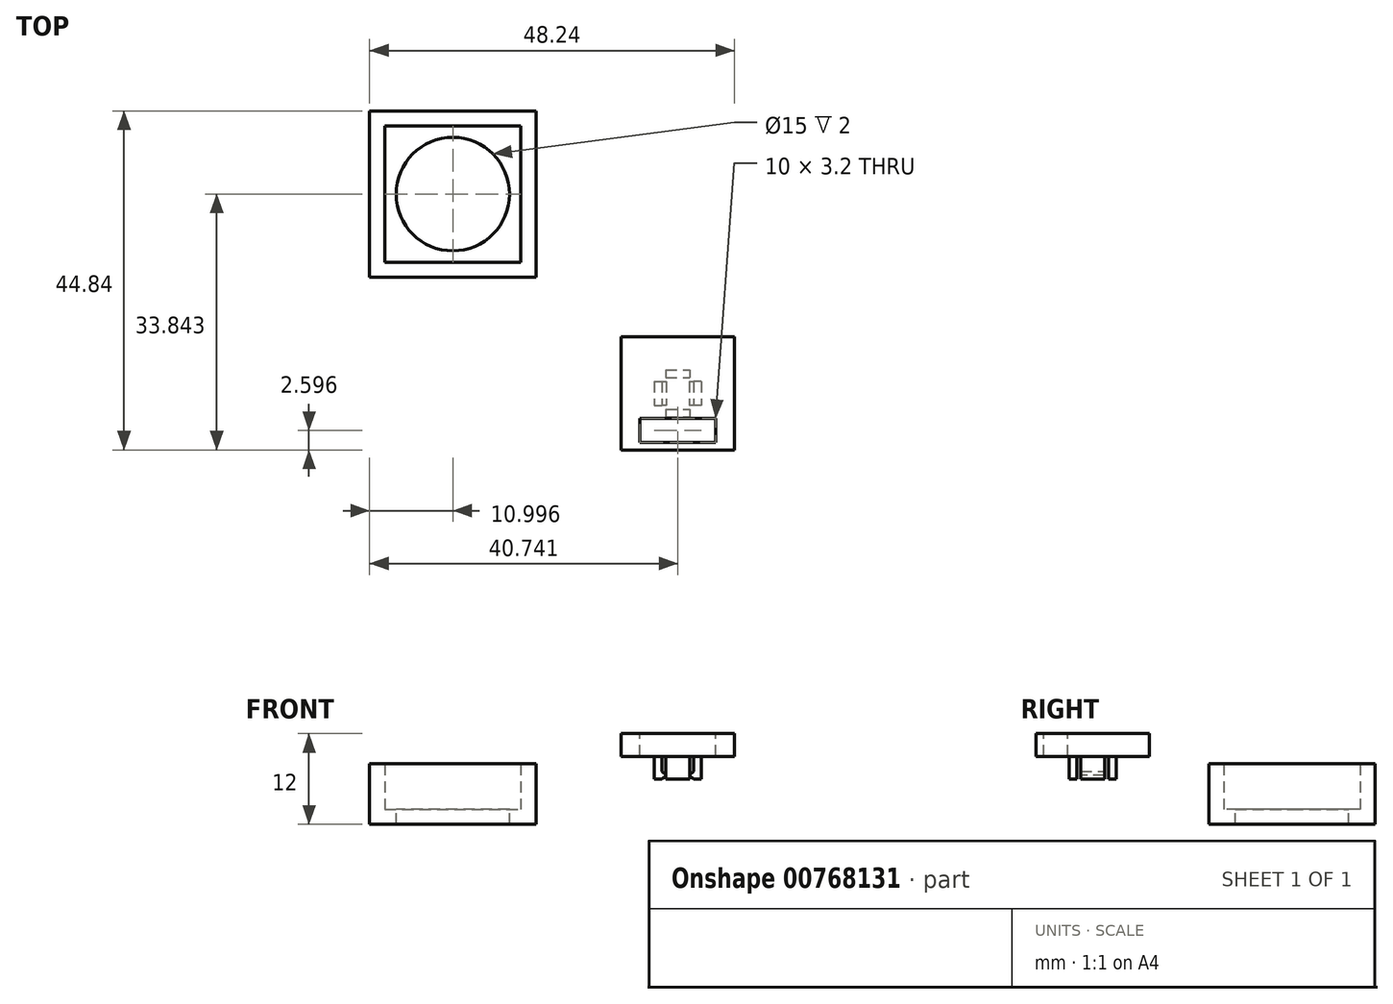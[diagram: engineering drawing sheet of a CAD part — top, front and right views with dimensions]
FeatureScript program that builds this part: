
annotation { "Feature Type Name" : "Feature", "Feature Type Description" : "" }
export const myFeature = defineFeature(function(context is Context, id is Id, definition is map)
    precondition{}
    {
        {
            var Q0;
            Q0=qCreatedBy(makeId("Top.planeOp"),FACE);
            var sketch = newSketch(context, id + "F0", { "sketchPlane" : qUnion([Q0])});
            skCircle(sketch, "E0", {"center": v(-35.06, 11.64) * mm, "radius": 7.5 * mm});
            skLineSegment(sketch, "E1", {"start": v(-38.26, 11.64) * mm, "end": v(-31.97, 11.64) * mm, "construction": true});
            skLineSegment(sketch, "E2", {"start": v(-35.06, 15.87) * mm, "end": v(-35.06, 7.55) * mm, "construction": true});
            skLineSegment(sketch, "E3.bottom", {"start": v(-44.06, 20.64) * mm, "end": v(-26.06, 20.64) * mm});
            skLineSegment(sketch, "E3.top", {"start": v(-44.06, 2.64) * mm, "end": v(-26.06, 2.64) * mm});
            skLineSegment(sketch, "E3.left", {"start": v(-44.06, 20.64) * mm, "end": v(-44.06, 2.64) * mm});
            skLineSegment(sketch, "E3.right", {"start": v(-26.06, 20.64) * mm, "end": v(-26.06, 2.64) * mm});
            skLineSegment(sketch, "E4.bottom", {"start": v(-46.06, 22.64) * mm, "end": v(-24.06, 22.64) * mm});
            skLineSegment(sketch, "E4.top", {"start": v(-46.06, 0.64) * mm, "end": v(-24.06, 0.64) * mm});
            skLineSegment(sketch, "E4.left", {"start": v(-46.06, 22.64) * mm, "end": v(-46.06, 0.64) * mm});
            skLineSegment(sketch, "E4.right", {"start": v(-24.06, 22.64) * mm, "end": v(-24.06, 0.64) * mm});
            skSolve(sketch);
        }
        {
            var Q0;
            Q0=makeQuery(id+"F0.imprint","IMPRINT",FACE,{"disambiguationData":[TD([[makeQuery(id+"F0.imprint","IMPRINT",EDGE,{"derivedFrom":sQuery(id+"F0.wireOp",EDGE,"P6zJFxaA-fPif-yFot-hNpY-F2ilPQpi4qHW.bottom")}),1.0]])]});
            var Q1;
            Q1=makeQuery(id+"F0.imprint","IMPRINT",FACE,{"disambiguationData":[TD([[makeQuery(id+"F0.imprint","IMPRINT",EDGE,{"derivedFrom":sQuery(id+"F0.wireOp",EDGE,"E0")}),-1.0]])]});
            var Q2;
            Q2=makeQuery(id+"F0.imprint","IMPRINT",FACE,{"disambiguationData":[TD([[makeQuery(id+"F0.imprint","IMPRINT",EDGE,{"derivedFrom":sQuery(id+"F0.wireOp",EDGE,"E3.bottom")}),1.0]])]});
            extrude(context, id + "F1", {"entities" : qUnion([Q0, Q1, Q2]), "oppositeDirection" : true, "depth" : 2 * mm, "offsetDistance" : 25 * mm});
        }
        {
            var Q0;
            Q0=makeQuery(id+"F0.imprint","IMPRINT",FACE,{"disambiguationData":[TD([[makeQuery(id+"F0.imprint","IMPRINT",EDGE,{"derivedFrom":sQuery(id+"F0.wireOp",EDGE,"E3.bottom")}),1.0]])]});
            extrude(context, id + "F2", {"entities" : qUnion([Q0]), "operationType" : NewBodyOperationType.ADD, "depth" : 6 * mm, "offsetDistance" : 25 * mm});
        }
        {
            var Q0;
            Q0=qCreatedBy(makeId("Top.planeOp"),FACE);
            var sketch = newSketch(context, id + "F3", { "sketchPlane" : qUnion([Q0])});
            skLineSegment(sketch, "E5.bottom", {"start": v(-7.32, -12.7) * mm, "end": v(-3.32, -12.7) * mm, "construction": true});
            skLineSegment(sketch, "E5.top", {"start": v(-7.32, -16.7) * mm, "end": v(-3.32, -16.7) * mm, "construction": true});
            skLineSegment(sketch, "E5.left", {"start": v(-7.32, -12.7) * mm, "end": v(-7.32, -16.7) * mm, "construction": true});
            skLineSegment(sketch, "E5.right", {"start": v(-3.32, -12.7) * mm, "end": v(-3.32, -16.7) * mm, "construction": true});
            skLineSegment(sketch, "E6.bottom", {"start": v(-12.82, -7.2) * mm, "end": v(2.18, -7.2) * mm});
            skLineSegment(sketch, "E6.top", {"start": v(-12.82, -22.2) * mm, "end": v(2.18, -22.2) * mm});
            skLineSegment(sketch, "E6.left", {"start": v(-12.82, -7.2) * mm, "end": v(-12.82, -22.2) * mm});
            skLineSegment(sketch, "E6.right", {"start": v(2.18, -7.2) * mm, "end": v(2.18, -22.2) * mm});
            skLineSegment(sketch, "E7", {"start": v(-5.32, -2.75) * mm, "end": v(-5.32, -34.44) * mm, "construction": true});
            skLineSegment(sketch, "E8", {"start": v(9.88, -14.7) * mm, "end": v(-20.88, -14.7) * mm, "construction": true});
            skCircle(sketch, "E9", {"center": v(-5.32, -19.6) * mm, "radius": 1.5 * mm, "construction": true});
            skLineSegment(sketch, "E10.bottom", {"start": v(-10.32, -18) * mm, "end": v(-0.32, -18) * mm});
            skLineSegment(sketch, "E10.top", {"start": v(-10.32, -21.2) * mm, "end": v(-0.32, -21.2) * mm});
            skLineSegment(sketch, "E10.left", {"start": v(-10.32, -18) * mm, "end": v(-10.32, -21.2) * mm});
            skLineSegment(sketch, "E10.right", {"start": v(-0.32, -18) * mm, "end": v(-0.32, -21.2) * mm});
            skLineSegment(sketch, "E11", {"start": v(4.65, -19.6) * mm, "end": v(-12.26, -19.6) * mm, "construction": true});
            skLineSegment(sketch, "E12.bottom", {"start": v(-8.42, -13.1) * mm, "end": v(-7.42, -13.1) * mm});
            skLineSegment(sketch, "E12.top", {"start": v(-8.42, -16.3) * mm, "end": v(-7.42, -16.3) * mm});
            skLineSegment(sketch, "E12.left", {"start": v(-8.42, -13.1) * mm, "end": v(-8.42, -16.3) * mm});
            skLineSegment(sketch, "E12.right", {"start": v(-7.42, -13.1) * mm, "end": v(-7.42, -16.3) * mm});
            skLineSegment(sketch, "E13.bottom", {"start": v(-6.92, -11.6) * mm, "end": v(-3.72, -11.6) * mm});
            skLineSegment(sketch, "E13.top", {"start": v(-6.92, -12.6) * mm, "end": v(-3.72, -12.6) * mm});
            skLineSegment(sketch, "E13.left", {"start": v(-3.72, -11.6) * mm, "end": v(-3.72, -12.6) * mm});
            skLineSegment(sketch, "E13.right", {"start": v(-6.92, -11.6) * mm, "end": v(-6.92, -12.6) * mm});
            skLineSegment(sketch, "E14.MirrorCS", {"start": v(-6.92, -16.8) * mm, "end": v(-3.72, -16.8) * mm});
            skLineSegment(sketch, "E15.MirrorCS", {"start": v(-6.92, -17.8) * mm, "end": v(-6.92, -16.8) * mm});
            skLineSegment(sketch, "E16.MirrorCS", {"start": v(-6.92, -17.8) * mm, "end": v(-3.72, -17.8) * mm});
            skLineSegment(sketch, "E17.MirrorCS", {"start": v(-3.72, -17.8) * mm, "end": v(-3.72, -16.8) * mm});
            skLineSegment(sketch, "E18.MirrorCS", {"start": v(-3.22, -13.1) * mm, "end": v(-3.22, -16.3) * mm});
            skLineSegment(sketch, "E19.MirrorCS", {"start": v(-2.22, -13.1) * mm, "end": v(-3.22, -13.1) * mm});
            skLineSegment(sketch, "E20.MirrorCS", {"start": v(-2.22, -13.1) * mm, "end": v(-2.22, -16.3) * mm});
            skLineSegment(sketch, "E21.MirrorCS", {"start": v(-2.22, -16.3) * mm, "end": v(-3.22, -16.3) * mm});
            skSolve(sketch);
        }
        {
            var Q0;
            Q0=qCreatedBy(makeId("Top.planeOp"),FACE);
            cPlane(context, id + "F4", {"entities" : qUnion([Q0]), "cplaneType" : CPlaneType.OFFSET, "offset" : 10 * mm, "width" : 150 * mm, "height" : 150 * mm});
        }
        {
            var Q0;
            Q0=qCreatedBy(id+"F4.planeOp",FACE);
            var sketch = newSketch(context, id + "F5", { "sketchPlane" : qUnion([Q0])});
            skLineSegment(sketch, "E22.bottom", {"start": v(-12.82, -7.2) * mm, "end": v(2.18, -7.2) * mm});
            skLineSegment(sketch, "E22.top", {"start": v(-12.82, -22.2) * mm, "end": v(2.18, -22.2) * mm});
            skLineSegment(sketch, "E22.left", {"start": v(-12.82, -7.2) * mm, "end": v(-12.82, -22.2) * mm});
            skLineSegment(sketch, "E22.right", {"start": v(2.18, -7.2) * mm, "end": v(2.18, -22.2) * mm});
            skLineSegment(sketch, "E23.bottom", {"start": v(-10.32, -18) * mm, "end": v(-0.32, -18) * mm});
            skLineSegment(sketch, "E23.top", {"start": v(-10.32, -21.2) * mm, "end": v(-0.32, -21.2) * mm});
            skLineSegment(sketch, "E23.left", {"start": v(-10.32, -18) * mm, "end": v(-10.32, -21.2) * mm});
            skLineSegment(sketch, "E23.right", {"start": v(-0.32, -18) * mm, "end": v(-0.32, -21.2) * mm});
            skSolve(sketch);
        }
        {
            var Q0;
            Q0=qCreatedBy(id+"F4.planeOp",FACE);
            cPlane(context, id + "F6", {"entities" : qUnion([Q0]), "cplaneType" : CPlaneType.OFFSET, "offset" : 3 * mm, "oppositeDirection" : true, "width" : 150 * mm, "height" : 150 * mm});
        }
        {
            var Q0;
            Q0=qCreatedBy(id+"F6.planeOp",FACE);
            var sketch = newSketch(context, id + "F7", { "sketchPlane" : qUnion([Q0])});
            skLineSegment(sketch, "E24.bottom", {"start": v(-6.92, -11.6) * mm, "end": v(-3.72, -11.6) * mm});
            skLineSegment(sketch, "E24.top", {"start": v(-6.92, -12.6) * mm, "end": v(-3.72, -12.6) * mm});
            skLineSegment(sketch, "E24.left", {"start": v(-6.92, -11.6) * mm, "end": v(-6.92, -12.6) * mm});
            skLineSegment(sketch, "E24.right", {"start": v(-3.72, -11.6) * mm, "end": v(-3.72, -12.6) * mm});
            skLineSegment(sketch, "E25.bottom", {"start": v(-2.22, -13.1) * mm, "end": v(-3.22, -13.1) * mm});
            skLineSegment(sketch, "E25.top", {"start": v(-2.22, -16.3) * mm, "end": v(-3.22, -16.3) * mm});
            skLineSegment(sketch, "E25.left", {"start": v(-2.22, -13.1) * mm, "end": v(-2.22, -16.3) * mm});
            skLineSegment(sketch, "E25.right", {"start": v(-3.22, -13.1) * mm, "end": v(-3.22, -16.3) * mm});
            skLineSegment(sketch, "E26.bottom", {"start": v(-6.92, -16.8) * mm, "end": v(-3.72, -16.8) * mm});
            skLineSegment(sketch, "E26.top", {"start": v(-6.92, -17.8) * mm, "end": v(-3.72, -17.8) * mm});
            skLineSegment(sketch, "E26.left", {"start": v(-6.92, -16.8) * mm, "end": v(-6.92, -17.8) * mm});
            skLineSegment(sketch, "E26.right", {"start": v(-3.72, -16.8) * mm, "end": v(-3.72, -17.8) * mm});
            skLineSegment(sketch, "E27.bottom", {"start": v(-8.42, -13.1) * mm, "end": v(-7.42, -13.1) * mm});
            skLineSegment(sketch, "E27.top", {"start": v(-8.42, -16.3) * mm, "end": v(-7.42, -16.3) * mm});
            skLineSegment(sketch, "E27.left", {"start": v(-8.42, -13.1) * mm, "end": v(-8.42, -16.3) * mm});
            skLineSegment(sketch, "E27.right", {"start": v(-7.42, -13.1) * mm, "end": v(-7.42, -16.3) * mm});
            skSolve(sketch);
        }
        {
            var Q0;
            Q0=qCreatedBy(id+"F6.planeOp",FACE);
            cPlane(context, id + "F8", {"entities" : qUnion([Q0]), "cplaneType" : CPlaneType.OFFSET, "offset" : 2 * mm, "oppositeDirection" : true, "width" : 150 * mm, "height" : 150 * mm});
        }
        {
            var Q0;
            Q0=qCreatedBy(id+"F8.planeOp",FACE);
            cPlane(context, id + "F9", {"entities" : qUnion([Q0]), "cplaneType" : CPlaneType.OFFSET, "offset" : 0.5 * mm, "oppositeDirection" : true, "width" : 150 * mm, "height" : 150 * mm});
        }
        {
            var Q0;
            Q0=qCreatedBy(id+"F9.planeOp",FACE);
            var sketch = newSketch(context, id + "F10", { "sketchPlane" : qUnion([Q0])});
            skLineSegment(sketch, "E28.bottom", {"start": v(-8.42, -13.1) * mm, "end": v(-6.82, -13.1) * mm});
            skLineSegment(sketch, "E28.top", {"start": v(-8.42, -16.3) * mm, "end": v(-6.82, -16.3) * mm});
            skLineSegment(sketch, "E28.left", {"start": v(-8.42, -13.1) * mm, "end": v(-8.42, -16.3) * mm});
            skLineSegment(sketch, "E28.right", {"start": v(-6.82, -13.1) * mm, "end": v(-6.82, -16.3) * mm});
            skLineSegment(sketch, "E29.MirrorCS", {"start": v(-3.82, -13.1) * mm, "end": v(-3.82, -16.3) * mm});
            skLineSegment(sketch, "E30.MirrorCS", {"start": v(-2.22, -13.1) * mm, "end": v(-3.82, -13.1) * mm});
            skLineSegment(sketch, "E31.MirrorCS", {"start": v(-2.22, -13.1) * mm, "end": v(-2.22, -16.3) * mm});
            skLineSegment(sketch, "E32.MirrorCS", {"start": v(-2.22, -16.3) * mm, "end": v(-3.82, -16.3) * mm});
            skLineSegment(sketch, "E33.bottom", {"start": v(-6.92, -11.6) * mm, "end": v(-3.72, -11.6) * mm});
            skLineSegment(sketch, "E33.top", {"start": v(-6.92, -12.6) * mm, "end": v(-3.72, -12.6) * mm});
            skLineSegment(sketch, "E33.left", {"start": v(-6.92, -11.6) * mm, "end": v(-6.92, -12.6) * mm});
            skLineSegment(sketch, "E33.right", {"start": v(-3.72, -11.6) * mm, "end": v(-3.72, -12.6) * mm});
            skLineSegment(sketch, "E34.bottom", {"start": v(-6.92, -16.8) * mm, "end": v(-3.72, -16.8) * mm});
            skLineSegment(sketch, "E34.top", {"start": v(-6.92, -17.8) * mm, "end": v(-3.72, -17.8) * mm});
            skLineSegment(sketch, "E34.left", {"start": v(-6.92, -16.8) * mm, "end": v(-6.92, -17.8) * mm});
            skLineSegment(sketch, "E34.right", {"start": v(-3.72, -16.8) * mm, "end": v(-3.72, -17.8) * mm});
            skSolve(sketch);
        }
        {
            var Q0;
            Q0=qCreatedBy(id+"F9.planeOp",FACE);
            cPlane(context, id + "F11", {"entities" : qUnion([Q0]), "cplaneType" : CPlaneType.OFFSET, "offset" : 0.5 * mm, "oppositeDirection" : true, "width" : 150 * mm, "height" : 150 * mm});
        }
        {
            var Q0;
            Q0=qCreatedBy(id+"F11.planeOp",FACE);
            var sketch = newSketch(context, id + "F12", { "sketchPlane" : qUnion([Q0])});
            skLineSegment(sketch, "E35.bottom", {"start": v(-8.42, -16.3) * mm, "end": v(-7.42, -16.3) * mm});
            skLineSegment(sketch, "E35.top", {"start": v(-8.42, -13.1) * mm, "end": v(-7.42, -13.1) * mm});
            skLineSegment(sketch, "E35.left", {"start": v(-8.42, -16.3) * mm, "end": v(-8.42, -13.1) * mm});
            skLineSegment(sketch, "E35.right", {"start": v(-7.42, -16.3) * mm, "end": v(-7.42, -13.1) * mm});
            skLineSegment(sketch, "E36.bottom", {"start": v(-3.22, -16.3) * mm, "end": v(-2.22, -16.3) * mm});
            skLineSegment(sketch, "E36.top", {"start": v(-3.22, -13.1) * mm, "end": v(-2.22, -13.1) * mm});
            skLineSegment(sketch, "E36.left", {"start": v(-3.22, -16.3) * mm, "end": v(-3.22, -13.1) * mm});
            skLineSegment(sketch, "E36.right", {"start": v(-2.22, -16.3) * mm, "end": v(-2.22, -13.1) * mm});
            skLineSegment(sketch, "E37.bottom", {"start": v(-3.72, -12.6) * mm, "end": v(-6.92, -12.6) * mm});
            skLineSegment(sketch, "E37.top", {"start": v(-3.72, -11.6) * mm, "end": v(-6.92, -11.6) * mm});
            skLineSegment(sketch, "E37.left", {"start": v(-3.72, -12.6) * mm, "end": v(-3.72, -11.6) * mm});
            skLineSegment(sketch, "E37.right", {"start": v(-6.92, -12.6) * mm, "end": v(-6.92, -11.6) * mm});
            skLineSegment(sketch, "E38.bottom", {"start": v(-6.92, -17.8) * mm, "end": v(-3.72, -17.8) * mm});
            skLineSegment(sketch, "E38.top", {"start": v(-6.92, -16.8) * mm, "end": v(-3.72, -16.8) * mm});
            skLineSegment(sketch, "E38.left", {"start": v(-6.92, -17.8) * mm, "end": v(-6.92, -16.8) * mm});
            skLineSegment(sketch, "E38.right", {"start": v(-3.72, -17.8) * mm, "end": v(-3.72, -16.8) * mm});
            skSolve(sketch);
        }
        {
            var Q0;
            Q0=makeQuery(id+"F5.imprint","IMPRINT",FACE,{"disambiguationData":[TD([[makeQuery(id+"F5.imprint","IMPRINT",EDGE,{"derivedFrom":sQuery(id+"F5.wireOp",EDGE,"E22.bottom")}),-1.0]])]});
            var Q1;
            Q1=qCreatedBy(id+"F6.planeOp",FACE);
            extrude(context, id + "F13", {"entities" : qUnion([Q0]), "endBound" : BoundingType.UP_TO_SURFACE, "oppositeDirection" : true, "depth" : 25 * mm, "endBoundEntityFace" : qUnion([Q1]), "offsetDistance" : 25 * mm});
        }
        {
            var Q0;
            Q0 = qSketchRegion(id + "F7", true);
            var Q1;
            Q1=qCreatedBy(id+"F8.planeOp",FACE);
            extrude(context, id + "F14", {"entities" : qUnion([Q0]), "operationType" : NewBodyOperationType.ADD, "endBound" : BoundingType.UP_TO_SURFACE, "oppositeDirection" : true, "depth" : 25 * mm, "endBoundEntityFace" : qUnion([Q1]), "offsetDistance" : 25 * mm});
        }
        {
            var Q1;
            Q1=makeQuery(id+"F14.opExtrude","CAP_FACE",FACE,{"disambiguationData":[OSD([sQuery(id+"F7.wireOp",EDGE,"E25.bottom"),sQuery(id+"F7.wireOp",EDGE,"E25.top"),sQuery(id+"F7.wireOp",EDGE,"E25.left"),sQuery(id+"F7.wireOp",EDGE,"E25.right")])],"isStart":false});
            var Q2;
            Q2=makeQuery(id+"F10.imprint","IMPRINT",FACE,{"disambiguationData":[TD([[makeQuery(id+"F10.imprint","IMPRINT",EDGE,{"derivedFrom":sQuery(id+"F10.wireOp",EDGE,"E29.MirrorCS")}),1.0]])]});
            loft(context, id + "F15", {"operationType" : NewBodyOperationType.ADD, "sheetProfilesArray" : [{ "sheetProfileEntities" : qUnion([Q1]) }, { "sheetProfileEntities" : qUnion([Q2]) }]});
        }
        {
            var Q1;
            Q1=makeQuery(id+"F14.opExtrude","CAP_FACE",FACE,{"disambiguationData":[OSD([sQuery(id+"F7.wireOp",EDGE,"E27.bottom"),sQuery(id+"F7.wireOp",EDGE,"E27.top"),sQuery(id+"F7.wireOp",EDGE,"E27.left"),sQuery(id+"F7.wireOp",EDGE,"E27.right")])],"isStart":false});
            var Q2;
            Q2=makeQuery(id+"F10.imprint","IMPRINT",FACE,{"disambiguationData":[TD([[makeQuery(id+"F10.imprint","IMPRINT",EDGE,{"derivedFrom":sQuery(id+"F10.wireOp",EDGE,"E28.bottom")}),-1.0]])]});
            loft(context, id + "F16", {"operationType" : NewBodyOperationType.ADD, "sheetProfilesArray" : [{ "sheetProfileEntities" : qUnion([Q1]) }, { "sheetProfileEntities" : qUnion([Q2]) }]});
        }
        {
            var Q0;
            Q0=makeQuery(id+"F14.opExtrude","CAP_FACE",FACE,{"disambiguationData":[OSD([sQuery(id+"F7.wireOp",EDGE,"E24.bottom"),sQuery(id+"F7.wireOp",EDGE,"E24.top"),sQuery(id+"F7.wireOp",EDGE,"E24.left"),sQuery(id+"F7.wireOp",EDGE,"E24.right")])],"isStart":false});
            var Q1;
            Q1=makeQuery(id+"F14.opExtrude","CAP_FACE",FACE,{"disambiguationData":[OSD([sQuery(id+"F7.wireOp",EDGE,"E26.bottom"),sQuery(id+"F7.wireOp",EDGE,"E26.top"),sQuery(id+"F7.wireOp",EDGE,"E26.left"),sQuery(id+"F7.wireOp",EDGE,"E26.right")])],"isStart":false});
            var Q2;
            Q2=qCreatedBy(id+"F9.planeOp",FACE);
            extrude(context, id + "F17", {"entities" : qUnion([Q0, Q1]), "operationType" : NewBodyOperationType.ADD, "endBound" : BoundingType.UP_TO_SURFACE, "depth" : 25 * mm, "endBoundEntityFace" : qUnion([Q2]), "offsetDistance" : 25 * mm});
        }
        {
            var Q1;
            Q1=makeQuery(id+"F15.opLoft","CAP_FACE",FACE,{"disambiguationData":[OSD([makeQuery(id+"F10.imprint","IMPRINT",FACE,{"disambiguationData":[TD([[makeQuery(id+"F10.imprint","IMPRINT",EDGE,{"derivedFrom":sQuery(id+"F10.wireOp",EDGE,"E29.MirrorCS")}),1.0]])]})])],"isStart":true});
            var Q2;
            Q2=makeQuery(id+"F12.imprint","IMPRINT",FACE,{"disambiguationData":[TD([[makeQuery(id+"F12.imprint","IMPRINT",EDGE,{"derivedFrom":sQuery(id+"F12.wireOp",EDGE,"E36.bottom")}),1.0]])]});
            loft(context, id + "F18", {"operationType" : NewBodyOperationType.ADD, "sheetProfilesArray" : [{ "sheetProfileEntities" : qUnion([Q1]) }, { "sheetProfileEntities" : qUnion([Q2]) }]});
        }
        {
            var Q1;
            Q1=makeQuery(id+"F16.opLoft","CAP_FACE",FACE,{"disambiguationData":[OSD([makeQuery(id+"F10.imprint","IMPRINT",FACE,{"disambiguationData":[TD([[makeQuery(id+"F10.imprint","IMPRINT",EDGE,{"derivedFrom":sQuery(id+"F10.wireOp",EDGE,"E28.bottom")}),-1.0]])]})])],"isStart":true});
            var Q2;
            Q2=makeQuery(id+"F12.imprint","IMPRINT",FACE,{"disambiguationData":[TD([[makeQuery(id+"F12.imprint","IMPRINT",EDGE,{"derivedFrom":sQuery(id+"F12.wireOp",EDGE,"E35.bottom")}),1.0]])]});
            loft(context, id + "F19", {"operationType" : NewBodyOperationType.ADD, "sheetProfilesArray" : [{ "sheetProfileEntities" : qUnion([Q1]) }, { "sheetProfileEntities" : qUnion([Q2]) }]});
        }
        {
            var Q0;
            Q0=makeQuery(id+"F17.opExtrude","CAP_FACE",FACE,{"disambiguationData":[OSD([sQuery(id+"F7.wireOp",EDGE,"E26.bottom"),sQuery(id+"F7.wireOp",EDGE,"E26.top"),sQuery(id+"F7.wireOp",EDGE,"E26.left"),sQuery(id+"F7.wireOp",EDGE,"E26.right")])],"isStart":false});
            var Q1;
            Q1=makeQuery(id+"F17.opExtrude","CAP_FACE",FACE,{"disambiguationData":[OSD([sQuery(id+"F7.wireOp",EDGE,"E24.bottom"),sQuery(id+"F7.wireOp",EDGE,"E24.top"),sQuery(id+"F7.wireOp",EDGE,"E24.left"),sQuery(id+"F7.wireOp",EDGE,"E24.right")])],"isStart":false});
            var Q2;
            Q2=qCreatedBy(id+"F11.planeOp",FACE);
            extrude(context, id + "F20", {"entities" : qUnion([Q0, Q1]), "operationType" : NewBodyOperationType.ADD, "endBound" : BoundingType.UP_TO_SURFACE, "depth" : 25 * mm, "endBoundEntityFace" : qUnion([Q2]), "offsetDistance" : 25 * mm});
        }
    });
